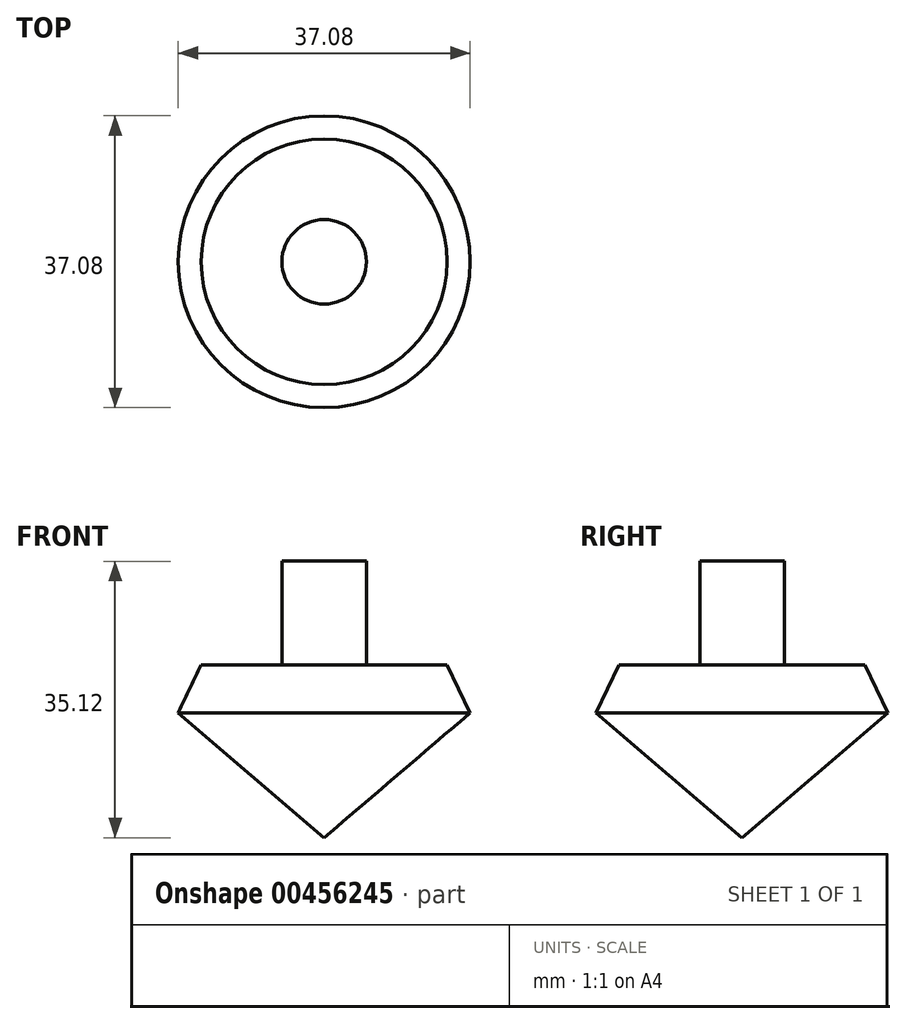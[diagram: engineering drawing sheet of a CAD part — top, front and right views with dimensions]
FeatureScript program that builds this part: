
annotation { "Feature Type Name" : "Feature", "Feature Type Description" : "" }
export const myFeature = defineFeature(function(context is Context, id is Id, definition is map)
    precondition{}
    {
        {
            var Q0;
            Q0=qCreatedBy(makeId("Front.planeOp"),FACE);
            var sketch = newSketch(context, id + "F0", { "sketchPlane" : qUnion([Q0])});
            skLineSegment(sketch, "E0", {"start": v(0, 44.15) * mm, "end": v(5.37, 44.15) * mm});
            skLineSegment(sketch, "E1", {"start": v(5.37, 44.15) * mm, "end": v(5.37, 30.98) * mm});
            skLineSegment(sketch, "E2", {"start": v(5.37, 30.98) * mm, "end": v(15.61, 30.98) * mm});
            skLineSegment(sketch, "E3", {"start": v(15.61, 30.98) * mm, "end": v(18.54, 24.88) * mm});
            skLineSegment(sketch, "E4", {"start": v(18.54, 24.88) * mm, "end": v(0, 9.03) * mm});
            skLineSegment(sketch, "E5", {"start": v(0, 9.03) * mm, "end": v(0, 44.15) * mm});
            skSolve(sketch);
        }
        {
            var Q0;
            Q0=makeQuery(id+"F0.imprint","IMPRINT",FACE,{"disambiguationData":[TD([[makeQuery(id+"F0.imprint","IMPRINT",EDGE,{"derivedFrom":sQuery(id+"F0.wireOp",EDGE,"E0")}),-1.0]])]});
            var Q1;
            Q1=sQuery(id+"F0.wireOp",EDGE,"E5");
            revolve(context, id + "F1", {"entities" : qUnion([Q0]), "axis" : qUnion([Q1]), "revolveType" : RevolveType.FULL});
        }
    });
